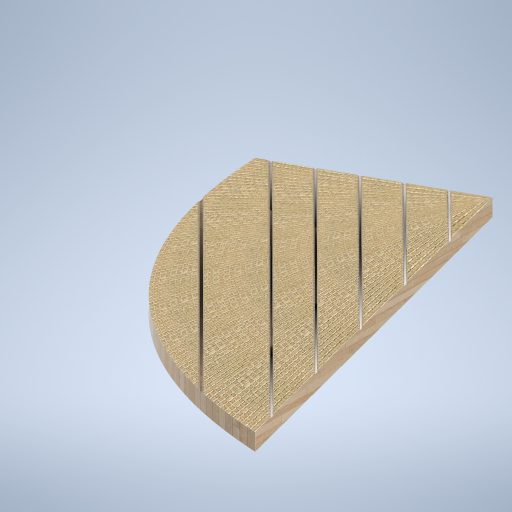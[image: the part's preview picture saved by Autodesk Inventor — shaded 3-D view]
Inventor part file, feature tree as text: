
AUTODESK INVENTOR PART (.ipt)
format: ipt  version: 2024.2 (Build 282272000, 272)  size: 1,029,632 bytes
history: native  units: mm
features: sketch x19, loft x7, plane x6, extrude x3, fillet x1
ambient origin geometry x8: Origin, YZ Plane, XZ Plane, XY Plane, X Axis, Y Axis, Z Axis, Center Point
bodies: Solid1 (feature_tree)
feature tree (36):
  sketch  "Sketch1"  dims[d6=2000.0mm d7=0.0mm d8=90.0deg d9=90.0deg d11=12.287118mm]
  plane  "Work Plane1"
  plane  "Work Plane2"
  plane  "Work Plane3"
  sketch  "Sketch2"  dims[d12=150.0mm d13=19.128809mm]
  plane  "Work Plane4"
  sketch  "Sketch3"  dims[d14=150.0mm d15=150.0mm]
  plane  "Work Plane5"
  loft  "Loft1"
  loft  "Loft2"
  loft  "Loft3"
  loft  "Loft4"
  loft  "Loft5"
  loft  "Loft6"
  plane  "Work Plane6"
  extrude  "Extrusion1"  TaperAngle=0.0deg  [1 undecoded]
  fillet  "Fillet1"  Radius=400.0mm
  sketch  "Sketch17"  dims[d46=20.0mm]
  extrude  "Extrusion3"  Depth=20.0mm
  extrude  "Extrusion4"  Depth=10.0mm
  loft  "Loft7"
  sketch  "Sketch4"  dims[d16=0.0mm d17=90.0deg d18=0.0mm d19=90.0deg]
  sketch  "Sketch5"  dims[d20=0.0mm d21=90.0deg d23=20.0mm]
  sketch  "Sketch6"  dims[d24=400.0mm d26=20.0mm]
  sketch  "Sketch7"  dims[d27=0.0mm d28=90.0deg d29=0.0mm d30=90.0deg d31=400.0mm]
  sketch  "Sketch8"  dims[d32=10.0mm d33=20.0mm]
  sketch  "Sketch9"  dims[d34=400.0mm d35=10.0mm]
  sketch  "Sketch10"  dims[d36=20.0mm d37=0.0mm d38=90.0deg]
  sketch  "Sketch11"  dims[d39=0.0mm d40=90.0deg]
  sketch  "Sketch12"  dims[d41=400.0mm]
  sketch  "Sketch13"  dims[d42=10.0mm]
  sketch  "Sketch14"  dims[d43=20.0mm]
  sketch  "Sketch15"  dims[d44=400.0mm]
  sketch  "Sketch16"  dims[d45=10.0mm]
  sketch  "Sketch18"  dims[d47=0.0mm d48=90.0deg]
  sketch  "Sketch19"  dims[d49=0.0mm d50=90.0deg d51=400.0mm d52=10.0mm d53=20.0mm d54=400.0mm d55=10.0mm d56=20.0mm d57=0.0mm d58=90.0deg d59=0.0mm d60=90.0deg d61=400.0mm d62=10.0mm d63=20.0mm d64=400.0mm d66=20.0mm d67=0.0mm d68=90.0deg d69=0.0mm d70=90.0deg d71=45.0deg d73=20.0mm d74=0.0mm d75=0.0mm d76=10.0mm d79=280.0mm d80=0.0mm d81=380.0mm d82=0.0mm d83=0.0mm d84=90.0deg d85=0.0mm d86=90.0deg]
note: 1 required parameter value undecoded (feature->parameter linkage not recoverable at this tier; creation-order binding heuristic only, values carry confidence <= 0.55)
